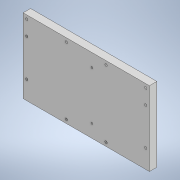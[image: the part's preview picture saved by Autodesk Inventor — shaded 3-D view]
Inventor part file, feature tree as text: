
AUTODESK INVENTOR PART (.ipt)
format: ipt  version: 2022.2 (Build 262287030, 287C)  size: 141,312 bytes
history: native  units: in
note: dims shown in document units (in); Inventor stores cm internally (conversion verified against a paired STEP export)
features: hole x3, sketch x3, extrude x1, projected_geometry x1
ambient origin geometry x8: Origin, YZ Plane, XZ Plane, XY Plane, X Axis, Y Axis, Z Axis, Center Point
bodies: Solid1 (feature_tree)
feature tree (8):
  extrude  "Extrusion1"  Depth=3.937in
  hole  "Hole1"  [1 undecoded]
  hole  "Hole2"  [1 undecoded]
  hole  "Hole3"  [1 undecoded]
  sketch  "Sketch1"  dims[d0=6.6929in d1=3.937in]
  projected_geometry  "Projected Loop1"
  sketch  "Sketch3"  dims[d2=0.3937in d3=0.0in d17=2.0997in]
  sketch  "Sketch4"  dims[d36=0.125in d37=0.2953in d38=0.1476in d39=0.0984in d40=90.0deg d41=0.1969in d42=0.0in d51=0.7874in d53=1.9685in d54=0.3937in d56=0.3937in d59=0.7874in d61=6.2992in d62=0.3937in d64=0.3937in d66=0.7874in d68=6.2992in d69=0.3937in d71=0.3937in d73=0.1969in d74=0.1969in d75=0.1969in d77=0.1969in d81=0.5906in d82=1.5748in d84=360.0deg d86=0.0984in d87=0.2953in d88=0.1476in d89=0.0984in d90=90.0deg d91=0.1181in d92=0.0in d94=1.2795in d95=0.7874in d97=2.5591in d98=0.3937in d100=0.3937in d102=0.0984in d103=0.315in d104=0.1476in d105=0.0984in d106=90.0deg d107=0.1181in d108=0.0in d109=3.6465in d110=0.7874in d112=2.0997in d113=0.7874in d115=3.5433in d118=0.9843in d4=0.3937in d5=0.3937in d6=0.3937in d7=0.0591in d8=0.0984in d9=0.1476in d10=0.5635in d11=0.2953in d12=0.8108in d13=0.0246in d14=0.2953in d15=0.1476in]
note: 3 required parameter values undecoded (feature->parameter linkage not recoverable at this tier; creation-order binding heuristic only, values carry confidence <= 0.55)
